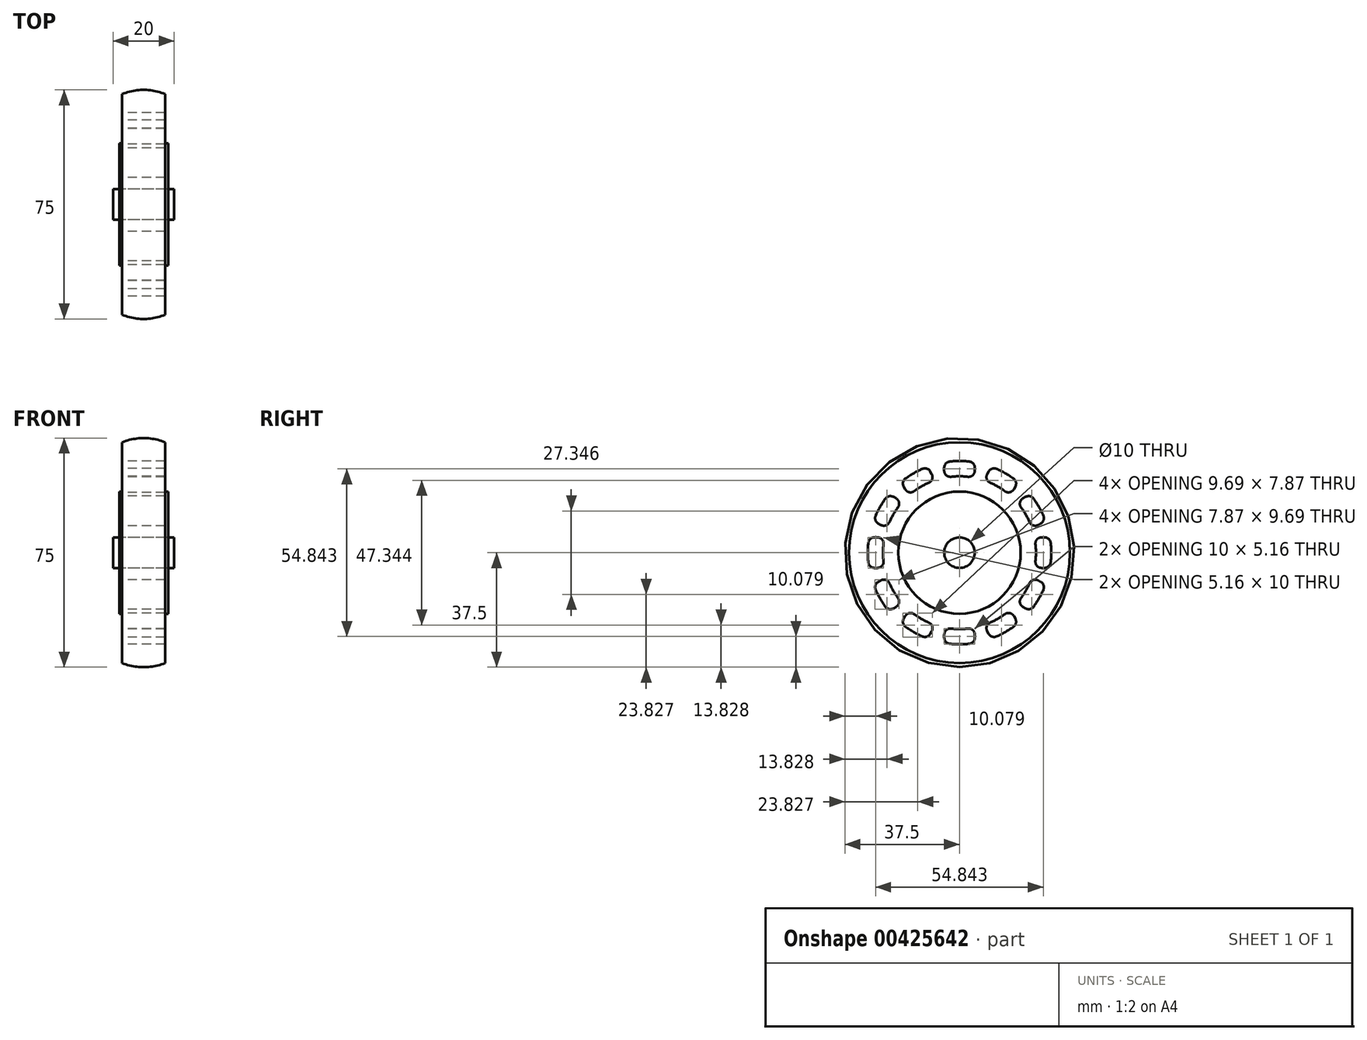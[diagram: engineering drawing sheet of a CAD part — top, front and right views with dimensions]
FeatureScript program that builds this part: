
annotation { "Feature Type Name" : "Feature", "Feature Type Description" : "" }
export const myFeature = defineFeature(function(context is Context, id is Id, definition is map)
    precondition{}
    {
        {
            var Q0;
            Q0=qCreatedBy(makeId("Right.planeOp"),FACE);
            var sketch = newSketch(context, id + "F0", { "sketchPlane" : qUnion([Q0])});
            skCircle(sketch, "E0", {"center": v(0, 0) * mm, "radius": 37.5 * mm});
            skCircle(sketch, "E1", {"center": v(0, 0) * mm, "radius": 35 * mm});
            skCircle(sketch, "E2", {"center": v(0, 0) * mm, "radius": 20 * mm});
            skCircle(sketch, "E3", {"center": v(0, 0) * mm, "radius": 5 * mm});
            skArc(sketch, "E4", {"start": v(-12.13, 27.44) * mm, "mid": v(-15, 25.98) * mm, "end": v(-17.7, 24.22) * mm});
            skArc(sketch, "E5", {"start": v(-10.02, 22.9) * mm, "mid": v(-12.5, 21.65) * mm, "end": v(-14.83, 20.13) * mm});
            skLineSegment(sketch, "E6", {"start": v(0, 0) * mm, "end": v(0, 37.5) * mm});
            skLineSegment(sketch, "E7.trimOffspring", {"start": v(-5, 26.83) * mm, "end": v(-5, 27.84) * mm});
            skLineSegment(sketch, "E8.trimOffspring", {"start": v(5, 26.83) * mm, "end": v(5, 27.84) * mm});
            skLineSegment(sketch, "E9.1.0", {"start": v(-17.75, 20.74) * mm, "end": v(-18.25, 21.6) * mm});
            skLineSegment(sketch, "E9.1.1", {"start": v(-9.09, 25.74) * mm, "end": v(-9.59, 26.6) * mm});
            skLineSegment(sketch, "E9.2.0", {"start": v(-25.74, 9.09) * mm, "end": v(-26.6, 9.59) * mm});
            skLineSegment(sketch, "E9.2.1", {"start": v(-20.74, 17.75) * mm, "end": v(-21.6, 18.25) * mm});
            skLineSegment(sketch, "E9.3.0", {"start": v(-26.83, -5) * mm, "end": v(-27.84, -5) * mm});
            skLineSegment(sketch, "E9.3.1", {"start": v(-26.83, 5) * mm, "end": v(-27.84, 5) * mm});
            skLineSegment(sketch, "E9.4.0", {"start": v(-20.74, -17.75) * mm, "end": v(-21.6, -18.25) * mm});
            skLineSegment(sketch, "E9.4.1", {"start": v(-25.74, -9.09) * mm, "end": v(-26.6, -9.59) * mm});
            skLineSegment(sketch, "E9.5.0", {"start": v(-9.09, -25.74) * mm, "end": v(-9.59, -26.6) * mm});
            skLineSegment(sketch, "E9.5.1", {"start": v(-17.75, -20.74) * mm, "end": v(-18.25, -21.6) * mm});
            skLineSegment(sketch, "E9.6.0", {"start": v(5, -26.83) * mm, "end": v(5, -27.84) * mm});
            skLineSegment(sketch, "E9.6.1", {"start": v(-5, -26.83) * mm, "end": v(-5, -27.84) * mm});
            skLineSegment(sketch, "E9.7.0", {"start": v(17.75, -20.74) * mm, "end": v(18.25, -21.6) * mm});
            skLineSegment(sketch, "E9.7.1", {"start": v(9.09, -25.74) * mm, "end": v(9.59, -26.6) * mm});
            skLineSegment(sketch, "E9.8.0", {"start": v(25.74, -9.09) * mm, "end": v(26.6, -9.59) * mm});
            skLineSegment(sketch, "E9.8.1", {"start": v(20.74, -17.75) * mm, "end": v(21.6, -18.25) * mm});
            skLineSegment(sketch, "E9.9.0", {"start": v(26.83, 5) * mm, "end": v(27.84, 5) * mm});
            skLineSegment(sketch, "E9.9.1", {"start": v(26.83, -5) * mm, "end": v(27.84, -5) * mm});
            skLineSegment(sketch, "E9.10.0", {"start": v(20.74, 17.75) * mm, "end": v(21.6, 18.25) * mm});
            skLineSegment(sketch, "E9.10.1", {"start": v(25.74, 9.09) * mm, "end": v(26.6, 9.59) * mm});
            skLineSegment(sketch, "E9.11.0", {"start": v(9.09, 25.74) * mm, "end": v(9.59, 26.6) * mm});
            skLineSegment(sketch, "E9.11.1", {"start": v(17.75, 20.74) * mm, "end": v(18.25, 21.6) * mm});
            skArc(sketch, "E10.trimOffspring", {"start": v(-24.22, 17.7) * mm, "mid": v(-25.98, 15) * mm, "end": v(-27.44, 12.13) * mm});
            skArc(sketch, "E11.trimOffspring", {"start": v(-20.13, 14.83) * mm, "mid": v(-21.65, 12.5) * mm, "end": v(-22.9, 10.02) * mm});
            skArc(sketch, "E12.trimOffspring", {"start": v(-29.83, 3.21) * mm, "mid": v(-30, 0) * mm, "end": v(-29.83, -3.21) * mm});
            skArc(sketch, "E13.trimOffspring", {"start": v(-24.85, 2.78) * mm, "mid": v(-25, 0) * mm, "end": v(-24.85, -2.78) * mm});
            skArc(sketch, "E14.trimOffspring", {"start": v(3.21, 29.83) * mm, "mid": v(0, 30) * mm, "end": v(-3.21, 29.83) * mm});
            skArc(sketch, "E15.trimOffspring", {"start": v(2.78, 24.85) * mm, "mid": v(0, 25) * mm, "end": v(-2.78, 24.85) * mm});
            skArc(sketch, "E16.trimOffspring", {"start": v(17.7, 24.22) * mm, "mid": v(15, 25.98) * mm, "end": v(12.13, 27.44) * mm});
            skArc(sketch, "E17.trimOffspring", {"start": v(14.83, 20.13) * mm, "mid": v(12.5, 21.65) * mm, "end": v(10.02, 22.9) * mm});
            skArc(sketch, "E18.trimOffspring", {"start": v(22.9, 10.02) * mm, "mid": v(21.65, 12.5) * mm, "end": v(20.13, 14.83) * mm});
            skArc(sketch, "E19.trimOffspring", {"start": v(27.44, 12.13) * mm, "mid": v(25.98, 15) * mm, "end": v(24.22, 17.7) * mm});
            skArc(sketch, "E20.trimOffspring", {"start": v(24.85, -2.78) * mm, "mid": v(25, 0) * mm, "end": v(24.85, 2.78) * mm});
            skArc(sketch, "E21.trimOffspring", {"start": v(29.83, -3.21) * mm, "mid": v(30, 0) * mm, "end": v(29.83, 3.21) * mm});
            skArc(sketch, "E22.trimOffspring", {"start": v(20.13, -14.83) * mm, "mid": v(21.65, -12.5) * mm, "end": v(22.9, -10.02) * mm});
            skArc(sketch, "E23.trimOffspring", {"start": v(24.22, -17.7) * mm, "mid": v(25.98, -15) * mm, "end": v(27.44, -12.13) * mm});
            skArc(sketch, "E24.trimOffspring", {"start": v(10.02, -22.9) * mm, "mid": v(12.5, -21.65) * mm, "end": v(14.83, -20.13) * mm});
            skArc(sketch, "E25.trimOffspring", {"start": v(12.13, -27.44) * mm, "mid": v(15, -25.98) * mm, "end": v(17.7, -24.22) * mm});
            skArc(sketch, "E26.trimOffspring", {"start": v(-2.78, -24.85) * mm, "mid": v(0, -25) * mm, "end": v(2.78, -24.85) * mm});
            skArc(sketch, "E27.trimOffspring", {"start": v(-3.21, -29.83) * mm, "mid": v(0, -30) * mm, "end": v(3.21, -29.83) * mm});
            skArc(sketch, "E28.trimOffspring", {"start": v(-14.83, -20.13) * mm, "mid": v(-12.5, -21.65) * mm, "end": v(-10.02, -22.9) * mm});
            skArc(sketch, "E29.trimOffspring", {"start": v(-17.7, -24.22) * mm, "mid": v(-15, -25.98) * mm, "end": v(-12.13, -27.44) * mm});
            skArc(sketch, "E30.trimOffspring", {"start": v(-22.9, -10.02) * mm, "mid": v(-21.65, -12.5) * mm, "end": v(-20.13, -14.83) * mm});
            skArc(sketch, "E31.trimOffspring", {"start": v(-27.44, -12.13) * mm, "mid": v(-25.98, -15) * mm, "end": v(-24.22, -17.7) * mm});
            skPoint(sketch, "E32.visualSharp", {"position": v(-19.12, 23.12) * mm});
            skArc(sketch, "E32.filletArc", {"start": v(-17.7, 24.22) * mm, "mid": v(-18.47, 23.02) * mm, "end": v(-18.25, 21.6) * mm});
            skPoint(sketch, "E33.visualSharp", {"position": v(-16.58, 18.71) * mm});
            skArc(sketch, "E33.filletArc", {"start": v(-17.75, 20.74) * mm, "mid": v(-16.42, 19.78) * mm, "end": v(-14.83, 20.13) * mm});
            skPoint(sketch, "E34.visualSharp", {"position": v(-7.92, 23.71) * mm});
            skArc(sketch, "E34.filletArc", {"start": v(-10.02, 22.9) * mm, "mid": v(-8.92, 24.11) * mm, "end": v(-9.09, 25.74) * mm});
            skPoint(sketch, "E35.visualSharp", {"position": v(-10.46, 28.12) * mm});
            skArc(sketch, "E35.filletArc", {"start": v(-9.59, 26.6) * mm, "mid": v(-10.7, 27.51) * mm, "end": v(-12.13, 27.44) * mm});
            skPoint(sketch, "E36.visualSharp", {"position": v(-23.12, 19.12) * mm});
            skArc(sketch, "E36.filletArc", {"start": v(-21.6, 18.25) * mm, "mid": v(-23.02, 18.47) * mm, "end": v(-24.22, 17.7) * mm});
            skPoint(sketch, "E37.visualSharp", {"position": v(-18.71, 16.58) * mm});
            skArc(sketch, "E37.filletArc", {"start": v(-20.13, 14.83) * mm, "mid": v(-19.78, 16.42) * mm, "end": v(-20.74, 17.75) * mm});
            skPoint(sketch, "E38.visualSharp", {"position": v(-23.71, 7.92) * mm});
            skArc(sketch, "E38.filletArc", {"start": v(-25.74, 9.09) * mm, "mid": v(-24.11, 8.92) * mm, "end": v(-22.9, 10.02) * mm});
            skPoint(sketch, "E39.visualSharp", {"position": v(-28.12, 10.46) * mm});
            skArc(sketch, "E39.filletArc", {"start": v(-27.44, 12.13) * mm, "mid": v(-27.51, 10.7) * mm, "end": v(-26.6, 9.59) * mm});
            skPoint(sketch, "E40.visualSharp", {"position": v(-29.58, 5) * mm});
            skArc(sketch, "E40.filletArc", {"start": v(-27.84, 5) * mm, "mid": v(-29.18, 4.49) * mm, "end": v(-29.83, 3.21) * mm});
            skPoint(sketch, "E41.visualSharp", {"position": v(-24.5, 5) * mm});
            skArc(sketch, "E41.filletArc", {"start": v(-24.85, 2.78) * mm, "mid": v(-25.34, 4.33) * mm, "end": v(-26.83, 5) * mm});
            skPoint(sketch, "E42.visualSharp", {"position": v(-24.5, -5) * mm});
            skArc(sketch, "E42.filletArc", {"start": v(-26.83, -5) * mm, "mid": v(-25.34, -4.33) * mm, "end": v(-24.85, -2.78) * mm});
            skPoint(sketch, "E43.visualSharp", {"position": v(-29.58, -5) * mm});
            skArc(sketch, "E43.filletArc", {"start": v(-29.83, -3.21) * mm, "mid": v(-29.18, -4.49) * mm, "end": v(-27.84, -5) * mm});
            skPoint(sketch, "E44.visualSharp", {"position": v(-28.12, -10.46) * mm});
            skArc(sketch, "E44.filletArc", {"start": v(-26.6, -9.59) * mm, "mid": v(-27.51, -10.7) * mm, "end": v(-27.44, -12.13) * mm});
            skPoint(sketch, "E45.visualSharp", {"position": v(-23.71, -7.92) * mm});
            skArc(sketch, "E45.filletArc", {"start": v(-22.9, -10.02) * mm, "mid": v(-24.11, -8.92) * mm, "end": v(-25.74, -9.09) * mm});
            skPoint(sketch, "E46.visualSharp", {"position": v(-23.12, -19.12) * mm});
            skArc(sketch, "E46.filletArc", {"start": v(-24.22, -17.7) * mm, "mid": v(-23.02, -18.47) * mm, "end": v(-21.6, -18.25) * mm});
            skPoint(sketch, "E47.visualSharp", {"position": v(-18.71, -16.58) * mm});
            skArc(sketch, "E47.filletArc", {"start": v(-20.74, -17.75) * mm, "mid": v(-19.78, -16.42) * mm, "end": v(-20.13, -14.83) * mm});
            skPoint(sketch, "E48.visualSharp", {"position": v(-16.58, -18.71) * mm});
            skArc(sketch, "E48.filletArc", {"start": v(-14.83, -20.13) * mm, "mid": v(-16.42, -19.78) * mm, "end": v(-17.75, -20.74) * mm});
            skPoint(sketch, "E49.visualSharp", {"position": v(-19.12, -23.12) * mm});
            skArc(sketch, "E49.filletArc", {"start": v(-18.25, -21.6) * mm, "mid": v(-18.47, -23.02) * mm, "end": v(-17.7, -24.22) * mm});
            skPoint(sketch, "E50.visualSharp", {"position": v(-7.92, -23.71) * mm});
            skArc(sketch, "E50.filletArc", {"start": v(-9.09, -25.74) * mm, "mid": v(-8.92, -24.11) * mm, "end": v(-10.02, -22.9) * mm});
            skPoint(sketch, "E51.visualSharp", {"position": v(-10.46, -28.12) * mm});
            skArc(sketch, "E51.filletArc", {"start": v(-12.13, -27.44) * mm, "mid": v(-10.7, -27.51) * mm, "end": v(-9.59, -26.6) * mm});
            skPoint(sketch, "E52.visualSharp", {"position": v(-5, -24.5) * mm});
            skArc(sketch, "E52.filletArc", {"start": v(-2.78, -24.85) * mm, "mid": v(-4.33, -25.34) * mm, "end": v(-5, -26.83) * mm});
            skPoint(sketch, "E53.visualSharp", {"position": v(5, -24.5) * mm});
            skArc(sketch, "E53.filletArc", {"start": v(5, -26.83) * mm, "mid": v(4.33, -25.34) * mm, "end": v(2.78, -24.85) * mm});
            skPoint(sketch, "E54.visualSharp", {"position": v(5, -29.58) * mm});
            skArc(sketch, "E54.filletArc", {"start": v(3.21, -29.83) * mm, "mid": v(4.49, -29.18) * mm, "end": v(5, -27.84) * mm});
            skPoint(sketch, "E55.visualSharp", {"position": v(-5, -29.58) * mm});
            skArc(sketch, "E55.filletArc", {"start": v(-5, -27.84) * mm, "mid": v(-4.49, -29.18) * mm, "end": v(-3.21, -29.83) * mm});
            skPoint(sketch, "E56.visualSharp", {"position": v(7.92, -23.71) * mm});
            skArc(sketch, "E56.filletArc", {"start": v(10.02, -22.9) * mm, "mid": v(8.92, -24.11) * mm, "end": v(9.09, -25.74) * mm});
            skPoint(sketch, "E57.visualSharp", {"position": v(10.46, -28.12) * mm});
            skArc(sketch, "E57.filletArc", {"start": v(9.59, -26.6) * mm, "mid": v(10.7, -27.51) * mm, "end": v(12.13, -27.44) * mm});
            skPoint(sketch, "E58.visualSharp", {"position": v(19.12, -23.12) * mm});
            skArc(sketch, "E58.filletArc", {"start": v(17.7, -24.22) * mm, "mid": v(18.47, -23.02) * mm, "end": v(18.25, -21.6) * mm});
            skPoint(sketch, "E59.visualSharp", {"position": v(16.58, -18.71) * mm});
            skArc(sketch, "E59.filletArc", {"start": v(17.75, -20.74) * mm, "mid": v(16.42, -19.78) * mm, "end": v(14.83, -20.13) * mm});
            skPoint(sketch, "E60.visualSharp", {"position": v(18.71, -16.58) * mm});
            skArc(sketch, "E60.filletArc", {"start": v(20.13, -14.83) * mm, "mid": v(19.78, -16.42) * mm, "end": v(20.74, -17.75) * mm});
            skPoint(sketch, "E61.visualSharp", {"position": v(23.12, -19.12) * mm});
            skArc(sketch, "E61.filletArc", {"start": v(21.6, -18.25) * mm, "mid": v(23.02, -18.47) * mm, "end": v(24.22, -17.7) * mm});
            skPoint(sketch, "E62.visualSharp", {"position": v(23.71, -7.92) * mm});
            skArc(sketch, "E62.filletArc", {"start": v(25.74, -9.09) * mm, "mid": v(24.11, -8.92) * mm, "end": v(22.9, -10.02) * mm});
            skPoint(sketch, "E63.visualSharp", {"position": v(28.12, -10.46) * mm});
            skArc(sketch, "E63.filletArc", {"start": v(27.44, -12.13) * mm, "mid": v(27.51, -10.7) * mm, "end": v(26.6, -9.59) * mm});
            skPoint(sketch, "E64.visualSharp", {"position": v(29.58, -5) * mm});
            skArc(sketch, "E64.filletArc", {"start": v(27.84, -5) * mm, "mid": v(29.18, -4.49) * mm, "end": v(29.83, -3.21) * mm});
            skPoint(sketch, "E65.visualSharp", {"position": v(24.5, -5) * mm});
            skArc(sketch, "E65.filletArc", {"start": v(24.85, -2.78) * mm, "mid": v(25.34, -4.33) * mm, "end": v(26.83, -5) * mm});
            skPoint(sketch, "E66.visualSharp", {"position": v(24.5, 5) * mm});
            skArc(sketch, "E66.filletArc", {"start": v(26.83, 5) * mm, "mid": v(25.34, 4.33) * mm, "end": v(24.85, 2.78) * mm});
            skPoint(sketch, "E67.visualSharp", {"position": v(29.58, 5) * mm});
            skArc(sketch, "E67.filletArc", {"start": v(29.83, 3.21) * mm, "mid": v(29.18, 4.49) * mm, "end": v(27.84, 5) * mm});
            skPoint(sketch, "E68.visualSharp", {"position": v(23.71, 7.92) * mm});
            skArc(sketch, "E68.filletArc", {"start": v(22.9, 10.02) * mm, "mid": v(24.11, 8.92) * mm, "end": v(25.74, 9.09) * mm});
            skPoint(sketch, "E69.visualSharp", {"position": v(28.12, 10.46) * mm});
            skArc(sketch, "E69.filletArc", {"start": v(26.6, 9.59) * mm, "mid": v(27.51, 10.7) * mm, "end": v(27.44, 12.13) * mm});
            skPoint(sketch, "E70.visualSharp", {"position": v(23.12, 19.12) * mm});
            skArc(sketch, "E70.filletArc", {"start": v(24.22, 17.7) * mm, "mid": v(23.02, 18.47) * mm, "end": v(21.6, 18.25) * mm});
            skPoint(sketch, "E71.visualSharp", {"position": v(18.71, 16.58) * mm});
            skArc(sketch, "E71.filletArc", {"start": v(20.74, 17.75) * mm, "mid": v(19.78, 16.42) * mm, "end": v(20.13, 14.83) * mm});
            skPoint(sketch, "E72.visualSharp", {"position": v(16.58, 18.71) * mm});
            skArc(sketch, "E72.filletArc", {"start": v(14.83, 20.13) * mm, "mid": v(16.42, 19.78) * mm, "end": v(17.75, 20.74) * mm});
            skPoint(sketch, "E73.visualSharp", {"position": v(19.12, 23.12) * mm});
            skArc(sketch, "E73.filletArc", {"start": v(18.25, 21.6) * mm, "mid": v(18.47, 23.02) * mm, "end": v(17.7, 24.22) * mm});
            skPoint(sketch, "E74.visualSharp", {"position": v(10.46, 28.12) * mm});
            skArc(sketch, "E74.filletArc", {"start": v(12.13, 27.44) * mm, "mid": v(10.7, 27.51) * mm, "end": v(9.59, 26.6) * mm});
            skPoint(sketch, "E75.visualSharp", {"position": v(7.92, 23.71) * mm});
            skArc(sketch, "E75.filletArc", {"start": v(9.09, 25.74) * mm, "mid": v(8.92, 24.11) * mm, "end": v(10.02, 22.9) * mm});
            skPoint(sketch, "E76.visualSharp", {"position": v(5, 24.5) * mm});
            skArc(sketch, "E76.filletArc", {"start": v(2.78, 24.85) * mm, "mid": v(4.33, 25.34) * mm, "end": v(5, 26.83) * mm});
            skPoint(sketch, "E77.visualSharp", {"position": v(5, 29.58) * mm});
            skArc(sketch, "E77.filletArc", {"start": v(5, 27.84) * mm, "mid": v(4.49, 29.18) * mm, "end": v(3.21, 29.83) * mm});
            skPoint(sketch, "E78.visualSharp", {"position": v(-5, 29.58) * mm});
            skArc(sketch, "E78.filletArc", {"start": v(-3.21, 29.83) * mm, "mid": v(-4.49, 29.18) * mm, "end": v(-5, 27.84) * mm});
            skPoint(sketch, "E79.visualSharp", {"position": v(-5, 24.5) * mm});
            skArc(sketch, "E79.filletArc", {"start": v(-5, 26.83) * mm, "mid": v(-4.33, 25.34) * mm, "end": v(-2.78, 24.85) * mm});
            skSolve(sketch);
        }
        {
            var Q0;
            Q0=makeQuery(id+"F0.imprint","IMPRINT",FACE,{"disambiguationData":[TD([[makeQuery(id+"F0.imprint","IMPRINT",EDGE,{"derivedFrom":sQuery(id+"F0.wireOp",EDGE,"E1")}),1.0]])]});
            var Q1;
            Q1=makeQuery(id+"F0.imprint","IMPRINT",FACE,{"disambiguationData":[TD([[makeQuery(id+"F0.imprint","IMPRINT",EDGE,{"derivedFrom":sQuery(id+"F0.wireOp",EDGE,"E2")}),1.0]])]});
            var Q2;
            Q2=makeQuery(id+"F0.imprint","IMPRINT",FACE,{"disambiguationData":[TD([[makeQuery(id+"F0.imprint","IMPRINT",EDGE,{"derivedFrom":sQuery(id+"F0.wireOp",EDGE,"E0")}),1.0]])]});
            extrude(context, id + "F1", {"entities" : qUnion([Q0, Q1, Q2]), "endBound" : BoundingType.SYMMETRIC, "depth" : 14 * mm});
        }
        {
            var Q0;
            Q0=makeQuery(id+"F0.imprint","IMPRINT",FACE,{"disambiguationData":[TD([[makeQuery(id+"F0.imprint","IMPRINT",EDGE,{"derivedFrom":sQuery(id+"F0.wireOp",EDGE,"E2")}),1.0]])]});
            extrude(context, id + "F2", {"entities" : qUnion([Q0]), "operationType" : NewBodyOperationType.ADD, "endBound" : BoundingType.SYMMETRIC, "depth" : 16 * mm});
        }
        {
            var Q0;
            Q0=qCreatedBy(makeId("Front.planeOp"),FACE);
            var sketch = newSketch(context, id + "F3", { "sketchPlane" : qUnion([Q0])});
            skLineSegment(sketch, "E80", {"start": v(0, 0) * mm, "end": v(0, 37.5) * mm, "construction": true});
            skLineSegment(sketch, "E81", {"start": v(-51.6, 0) * mm, "end": v(51.36, 0) * mm, "construction": true});
            skArc(sketch, "E82", {"start": v(0, 37.5) * mm, "mid": v(-3.57, 37.16) * mm, "end": v(-7, 36.14) * mm});
            skArc(sketch, "E83.MirrorCS", {"start": v(0, 37.5) * mm, "mid": v(3.57, 37.16) * mm, "end": v(7, 36.14) * mm});
            skLineSegment(sketch, "E84", {"start": v(0, 37.5) * mm, "end": v(-7, 37.5) * mm});
            skLineSegment(sketch, "E85", {"start": v(-7, 36.14) * mm, "end": v(-7, 37.5) * mm});
            skLineSegment(sketch, "E86.MirrorCS", {"start": v(0, 37.5) * mm, "end": v(7, 37.5) * mm});
            skLineSegment(sketch, "E87.MirrorCS", {"start": v(7, 36.14) * mm, "end": v(7, 37.5) * mm});
            skSolve(sketch);
        }
        {
            var Q0;
            Q0 = qSketchRegion(id + "F3", true);
            var Q1;
            Q1=sQuery(id+"F3.wireOp",EDGE,"E81");
            revolve(context, id + "F4", {"operationType" : NewBodyOperationType.REMOVE, "entities" : qUnion([Q0]), "axis" : qUnion([Q1]), "revolveType" : RevolveType.FULL, "oppositeDirection" : true});
        }
        {
            var Q0;
            Q0=makeQuery(id+"F0.imprint","IMPRINT",FACE,{"disambiguationData":[TD([[makeQuery(id+"F0.imprint","IMPRINT",EDGE,{"derivedFrom":sQuery(id+"F0.wireOp",EDGE,"E3")}),1.0]])]});
            extrude(context, id + "F5", {"entities" : qUnion([Q0]), "endBound" : BoundingType.SYMMETRIC, "depth" : 20 * mm});
        }
    });
